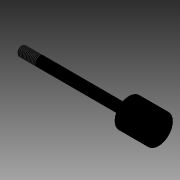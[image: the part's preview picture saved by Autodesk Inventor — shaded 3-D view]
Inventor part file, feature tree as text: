
AUTODESK INVENTOR PART (.ipt)
format: ipt  version: 2014 SP2 (Build 180246200, 246)  size: 144,384 bytes
history: native  units: in
note: dims shown in document units (in); Inventor stores cm internally (conversion verified against a paired STEP export)
features: other x91, revolve x3, sketch x3, thread x1
ambient origin geometry x8: Origin, YZ Plane, XZ Plane, XY Plane, X Axis, Y Axis, Z Axis, Center Point
bodies: Solid1 (feature_tree)
feature tree (98):
  revolve  "Revolution1"  Angle=360.0deg
  revolve  "Revolution2"  Angle=360.0deg
  thread  "Thread1"  [1 undecoded]
  revolve  "Revolution3"  [1 undecoded]
  other  "dia1_XY"
  other  "dia1_YZ"
  other  "dia1_ZX"
  other  "dia1_X"
  other  "dia1_Y"
  other  "dia1_Z"
  other  "dia1_Center"
  other  "dia12_XY"
  other  "dia12_YZ"
  other  "dia12_ZX"
  other  "dia12_X"
  other  "dia12_Y"
  other  "dia12_Z"
  other  "dia12_Center"
  other  "dia1r_XY"
  other  "dia1r_YZ"
  other  "dia1r_ZX"
  other  "dia1r_X"
  other  "dia1r_Y"
  other  "dia1r_Z"
  other  "dia1r_Center"
  other  "dia2_XY"
  other  "dia2_YZ"
  other  "dia2_ZX"
  other  "dia2_X"
  other  "dia2_Y"
  other  "dia2_Z"
  other  "dia2_Center"
  other  "dia22_XY"
  other  "dia22_YZ"
  other  "dia22_ZX"
  other  "dia22_X"
  other  "dia22_Y"
  other  "dia22_Z"
  other  "dia22_Center"
  other  "dia2r_XY"
  other  "dia2r_YZ"
  other  "dia2r_ZX"
  other  "dia2r_X"
  other  "dia2r_Y"
  other  "dia2r_Z"
  other  "dia2r_Center"
  other  "rl1_XY"
  other  "rl1_YZ"
  other  "rl1_ZX"
  other  "rl1_X"
  other  "rl1_Y"
  other  "rl1_Z"
  other  "rl1_Center"
  other  "rl2_XY"
  other  "rl2_YZ"
  other  "rl2_ZX"
  other  "rl2_X"
  other  "rl2_Y"
  other  "rl2_Z"
  other  "rl2_Center"
  other  "rod_cp_XY"
  other  "rod_cp_YZ"
  other  "rod_cp_ZX"
  other  "rod_cp_X"
  other  "rod_cp_Y"
  other  "rod_cp_Z"
  other  "rod_cp_Center"
  other  "stroke1_XY"
  other  "stroke1_YZ"
  other  "stroke1_ZX"
  other  "stroke1_X"
  other  "stroke1_Y"
  other  "stroke1_Z"
  other  "stroke1_Center"
  other  "thd1_XY"
  other  "thd1_YZ"
  other  "thd1_ZX"
  other  "thd1_X"
  other  "thd1_Y"
  other  "thd1_Z"
  other  "thd1_Center"
  other  "thd2_XY"
  other  "thd2_YZ"
  other  "thd2_ZX"
  other  "thd2_X"
  other  "thd2_Y"
  other  "thd2_Z"
  other  "thd2_Center"
  other  "to_rod_clevis_XY"
  other  "to_rod_clevis_YZ"
  other  "to_rod_clevis_ZX"
  other  "to_rod_clevis_X"
  other  "to_rod_clevis_Y"
  other  "to_rod_clevis_Z"
  other  "to_rod_clevis_Center"
  sketch  "Sketch_1"  dims[d0=360.0deg d1=360.0deg]
  sketch  "Sketch_3"  dims[d2=0.4787in d3=0.0in d4=360.0deg]
  sketch  "Sketch_30"  dims[d5=0.0in d6=0.0in d7=0.0in d8=0.0in d9=0.0in d10=0.0in]
note: 2 required parameter values undecoded (feature->parameter linkage not recoverable at this tier; creation-order binding heuristic only, values carry confidence <= 0.55)
